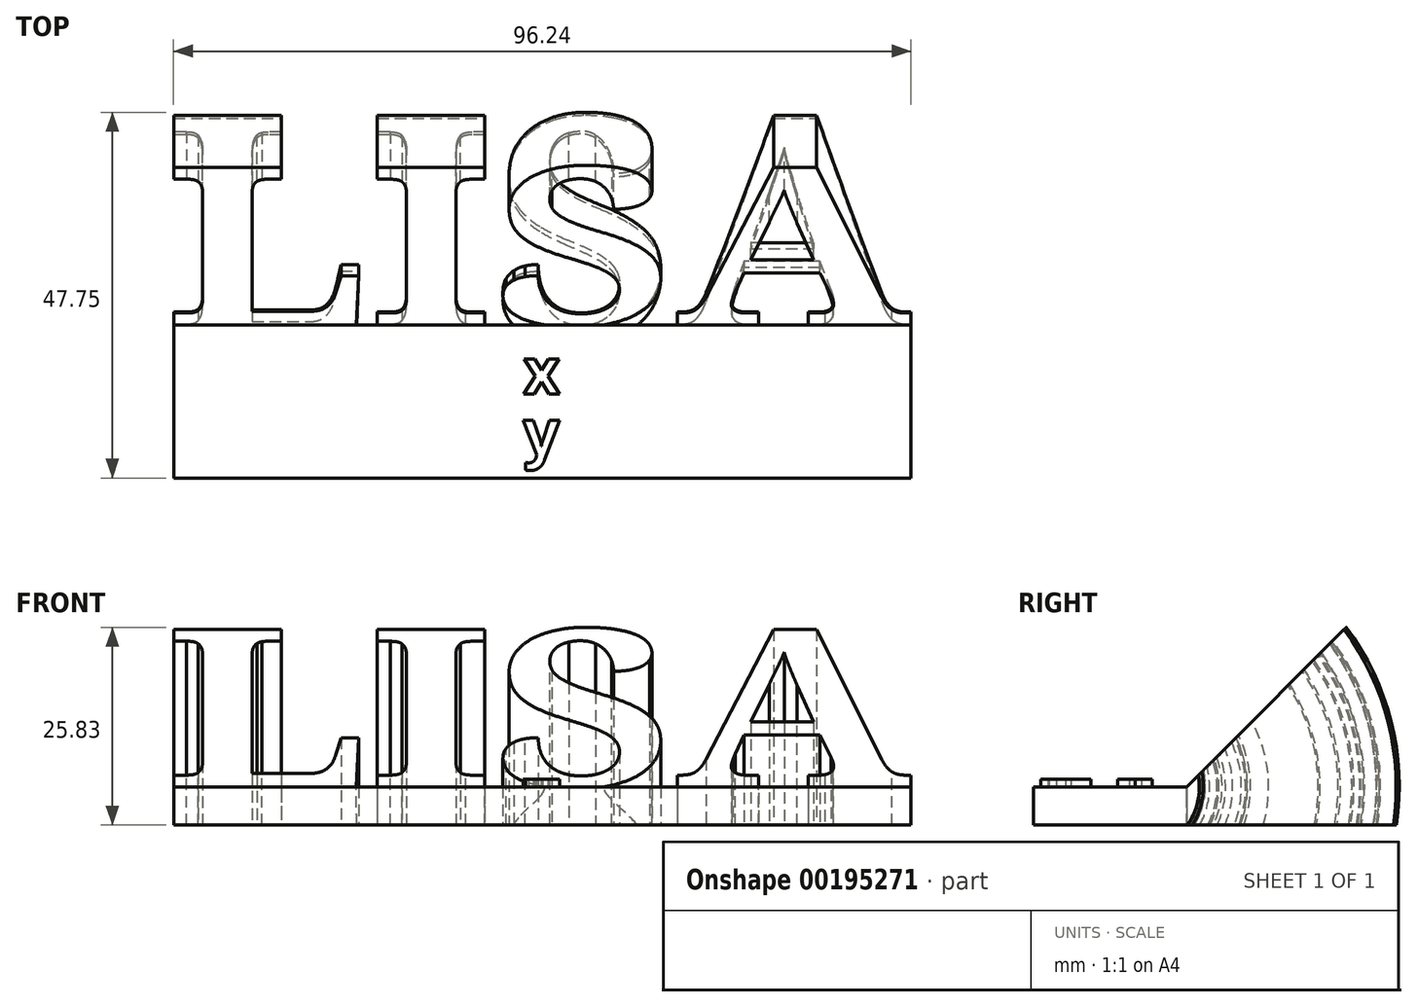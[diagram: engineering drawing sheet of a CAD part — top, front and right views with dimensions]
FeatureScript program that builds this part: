
annotation { "Feature Type Name" : "Feature", "Feature Type Description" : "" }
export const myFeature = defineFeature(function(context is Context, id is Id, definition is map)
    precondition{}
    {
        {
            var Q0;
            Q0=qCreatedBy(makeId("Top.planeOp"),FACE);
            var sketch = newSketch(context, id + "F0", { "sketchPlane" : qUnion([Q0])});
            skText(sketch, "E0", { "text": "LISA", "fontName": "NotoSerif-Bold.ttf"});
            const initialGuessF0  = {"E0": [-0.05146, -0.02176, 1, 0, 0.02929]};
            skSetInitialGuess(sketch, initialGuessF0);
            skSolve(sketch);
        }
        {
            var Q0;
            Q0=makeQuery(id+"F0.imprint","IMPRINT",FACE,{"disambiguationData":[TD([[makeQuery(id+"F0.imprint","IMPRINT",EDGE,{"derivedFrom":sQuery(id+"F0.wireOp",EDGE,"E0.sketch_text.stroke-28")}),-1.0]])]});
            cPlane(context, id + "F1", {"entities" : qUnion([Q0]), "cplaneType" : CPlaneType.OFFSET, "offset" : 5 * mm, "width" : 152.4 * mm, "height" : 152.4 * mm});
        }
        {
            var Q0;
            Q0=qCreatedBy(id+"F1.planeOp",FACE);
            var sketch = newSketch(context, id + "F2", { "sketchPlane" : qUnion([Q0])});
            skLineSegment(sketch, "E1", {"start": v(-39.35, -26.76) * mm, "end": v(46.8, -26.76) * mm});
            skSolve(sketch);
        }
        {
            var Q0;
            Q0=makeQuery(id+"F0.imprint","IMPRINT",FACE,{"disambiguationData":[TD([[makeQuery(id+"F0.imprint","IMPRINT",EDGE,{"derivedFrom":sQuery(id+"F0.wireOp",EDGE,"E0.sketch_text.stroke-0")}),-1.0]])]});
            var Q1;
            Q1=makeQuery(id+"F0.imprint","IMPRINT",FACE,{"disambiguationData":[TD([[makeQuery(id+"F0.imprint","IMPRINT",EDGE,{"derivedFrom":sQuery(id+"F0.wireOp",EDGE,"E0.sketch_text.stroke-28")}),-1.0]])]});
            var Q2;
            Q2=makeQuery(id+"F0.imprint","IMPRINT",FACE,{"disambiguationData":[TD([[makeQuery(id+"F0.imprint","IMPRINT",EDGE,{"derivedFrom":sQuery(id+"F0.wireOp",EDGE,"E0.sketch_text.stroke-56")}),-1.0]])]});
            var Q3;
            Q3=makeQuery(id+"F0.imprint","IMPRINT",FACE,{"disambiguationData":[TD([[makeQuery(id+"F0.imprint","IMPRINT",EDGE,{"derivedFrom":sQuery(id+"F0.wireOp",EDGE,"E0.sketch_text.stroke-112")}),-1.0]])]});
            var Q4;
            Q4=sQuery(id+"F2.wireOp",EDGE,"E1");
            revolve(context, id + "F3", {"entities" : qUnion([Q0, Q1, Q2, Q3]), "axis" : qUnion([Q4]), "revolveType" : RevolveType.ONE_DIRECTION, "angle" : 45 * degree});
        }
        {
            var Q0;
            Q0=qCreatedBy(makeId("Top.planeOp"),FACE);
            var sketch = newSketch(context, id + "F4", { "sketchPlane" : qUnion([Q0])});
            skLineSegment(sketch, "E2.bottom", {"start": v(-50.33, -19.69) * mm, "end": v(45.9, -19.69) * mm});
            skLineSegment(sketch, "E2.top", {"start": v(-50.33, -39.69) * mm, "end": v(45.9, -39.69) * mm});
            skLineSegment(sketch, "E2.left", {"start": v(-50.33, -19.69) * mm, "end": v(-50.33, -39.69) * mm});
            skLineSegment(sketch, "E2.right", {"start": v(45.9, -19.69) * mm, "end": v(45.9, -39.69) * mm});
            skSolve(sketch);
        }
        {
            var Q0;
            Q0=makeQuery(id+"F4.imprint","IMPRINT",FACE,{"disambiguationData":[TD([[makeQuery(id+"F4.imprint","IMPRINT",EDGE,{"derivedFrom":sQuery(id+"F4.wireOp",EDGE,"E2.bottom")}),-1.0]])]});
            extrude(context, id + "F5", {"entities" : qUnion([Q0]), "operationType" : NewBodyOperationType.ADD, "depth" : 5 * mm});
        }
        {
            var Q0;
            Q0=makeQuery(id+"F5.opExtrude","CAP_FACE",FACE,{"disambiguationData":[OSD([sQuery(id+"F4.wireOp",EDGE,"E2.bottom"),sQuery(id+"F4.wireOp",EDGE,"E2.top"),sQuery(id+"F4.wireOp",EDGE,"E2.left"),sQuery(id+"F4.wireOp",EDGE,"E2.right")])],"isStart":false});
            var sketch = newSketch(context, id + "F6", { "sketchPlane" : qUnion([Q0])});
            skText(sketch, "E3", { "text": "x", "fontName": "OpenSans-Bold.ttf"});
            skText(sketch, "E4", { "text": "y", "fontName": "OpenSans-Bold.ttf"});
            skLineSegment(sketch, "E5", {"start": v(-2.21, -39.69) * mm, "end": v(-1.93, -19.69) * mm, "construction": true});
            const initialGuessF6  = {"E3": [-0.00471, -0.02872, 1, 0, 0.006], "E4": [-0.0047, -0.03672, 1, 0, 0.006]};
            skSetInitialGuess(sketch, initialGuessF6);
            skSolve(sketch);
        }
        {
            var Q0;
            Q0 = qSketchRegion(id + "F6", true);
            extrude(context, id + "F7", {"entities" : qUnion([Q0]), "operationType" : NewBodyOperationType.ADD, "depth" : 1 * mm});
        }
    });
